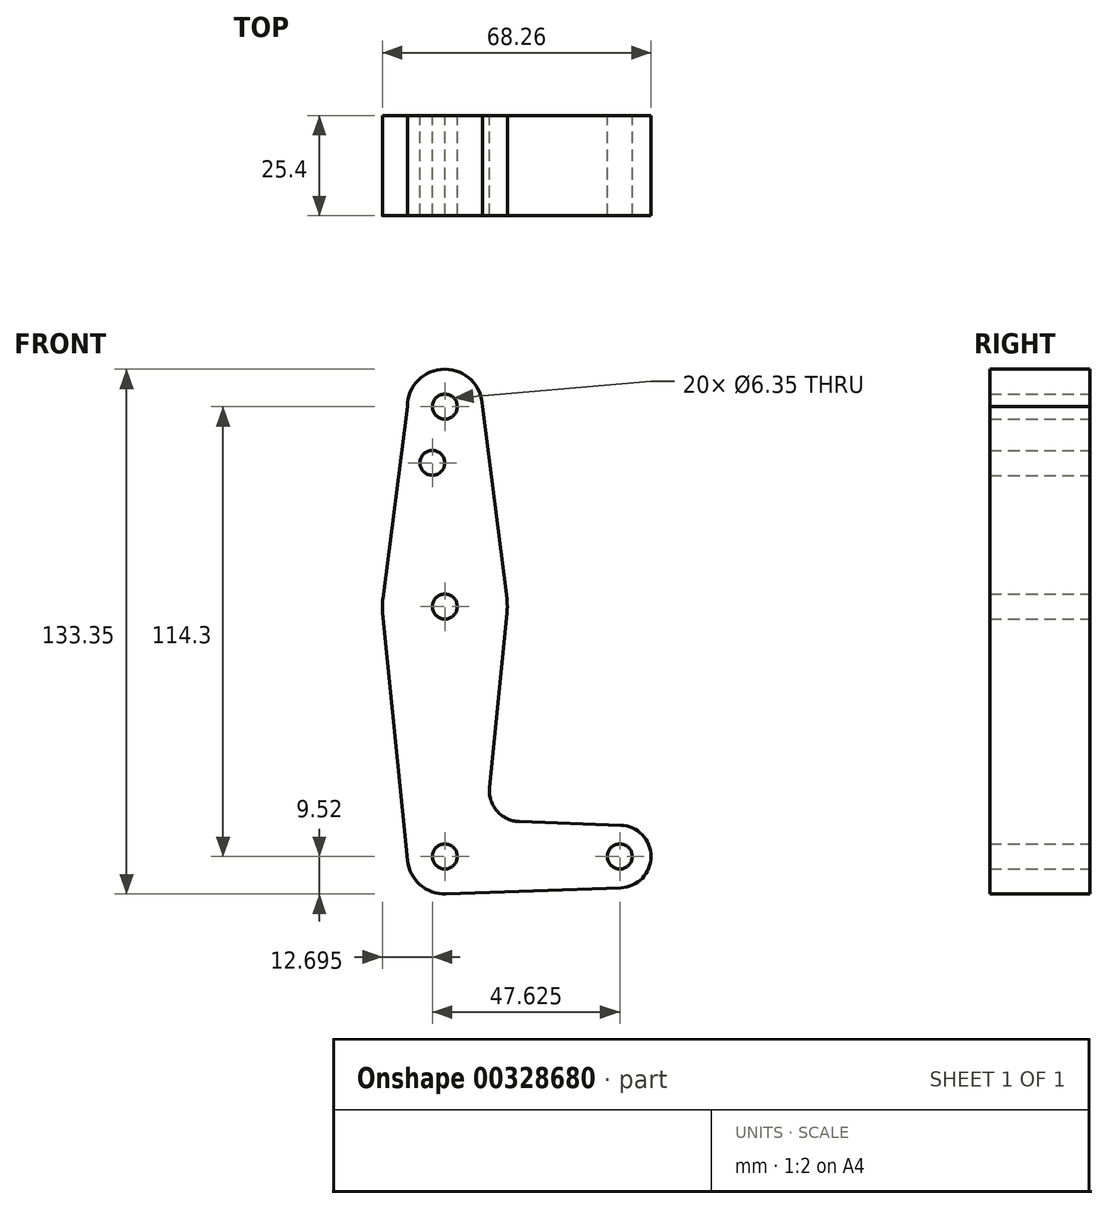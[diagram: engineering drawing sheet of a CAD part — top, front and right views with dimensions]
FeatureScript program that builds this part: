
annotation { "Feature Type Name" : "Feature", "Feature Type Description" : "" }
export const myFeature = defineFeature(function(context is Context, id is Id, definition is map)
    precondition{}
    {
        {
            var Q0;
            Q0=qCreatedBy(makeId("Front.planeOp"),FACE);
            var sketch = newSketch(context, id + "F0", { "sketchPlane" : qUnion([Q0])});
            skLineSegment(sketch, "E0", {"start": v(0, 0) * mm, "end": v(0, 114.3) * mm, "construction": true});
            skLineSegment(sketch, "E1", {"start": v(0, 0) * mm, "end": v(44.45, 0) * mm, "construction": true});
            skCircle(sketch, "E2", {"center": v(0, 0) * mm, "radius": 9.53 * mm});
            skCircle(sketch, "E3", {"center": v(44.45, 0) * mm, "radius": 7.94 * mm});
            skCircle(sketch, "E4", {"center": v(0, 63.5) * mm, "radius": 15.88 * mm});
            skCircle(sketch, "E5", {"center": v(0, 114.3) * mm, "radius": 9.53 * mm});
            skLineSegment(sketch, "E6", {"start": v(-9.53, 114.3) * mm, "end": v(-15.75, 65.5) * mm});
            skLineSegment(sketch, "E7", {"start": v(9.53, 114.3) * mm, "end": v(15.75, 65.5) * mm});
            skCircle(sketch, "E8", {"center": v(0, 0) * mm, "radius": 3.18 * mm});
            skCircle(sketch, "E9", {"center": v(0, 114.3) * mm, "radius": 3.18 * mm});
            skCircle(sketch, "E10", {"center": v(44.45, 0) * mm, "radius": 3.18 * mm});
            skCircle(sketch, "E11", {"center": v(0, 63.5) * mm, "radius": 3.18 * mm});
            skCircle(sketch, "E12", {"center": v(-3.17, 100.03) * mm, "radius": 3.18 * mm});
            skLineSegment(sketch, "E13", {"start": v(-15.8, 61.91) * mm, "end": v(-9.48, -0.95) * mm});
            skLineSegment(sketch, "E14", {"start": v(15.8, 61.91) * mm, "end": v(11.34, 17.6) * mm});
            skLineSegment(sketch, "E15", {"start": v(18.97, 8.85) * mm, "end": v(44.73, 7.93) * mm});
            skLineSegment(sketch, "E16", {"start": v(0.34, -9.52) * mm, "end": v(44.73, -7.93) * mm});
            skArc(sketch, "E17.filletArc", {"start": v(11.34, 17.6) * mm, "mid": v(13.26, 11.57) * mm, "end": v(18.97, 8.85) * mm});
            skSolve(sketch);
        }
        {
            var Q0;
            Q0 = qSketchRegion(id + "F0", true);
            extrude(context, id + "F1", {"entities" : qUnion([Q0]), "depth" : 25.4 * mm});
        }
        {
            var Q0;
            Q0 = qSketchRegion(id + "F0", true);
            extrude(context, id + "F2", {"entities" : qUnion([Q0]), "depth" : 25.4 * mm});
        }
        {
            var Q0;
            Q0 = qSketchRegion(id + "F0", true);
            extrude(context, id + "F3", {"entities" : qUnion([Q0]), "depth" : 25.4 * mm});
        }
        {
            var Q0;
            Q0 = qSketchRegion(id + "F0", true);
            extrude(context, id + "F4", {"entities" : qUnion([Q0]), "depth" : 25.4 * mm});
        }
    });
